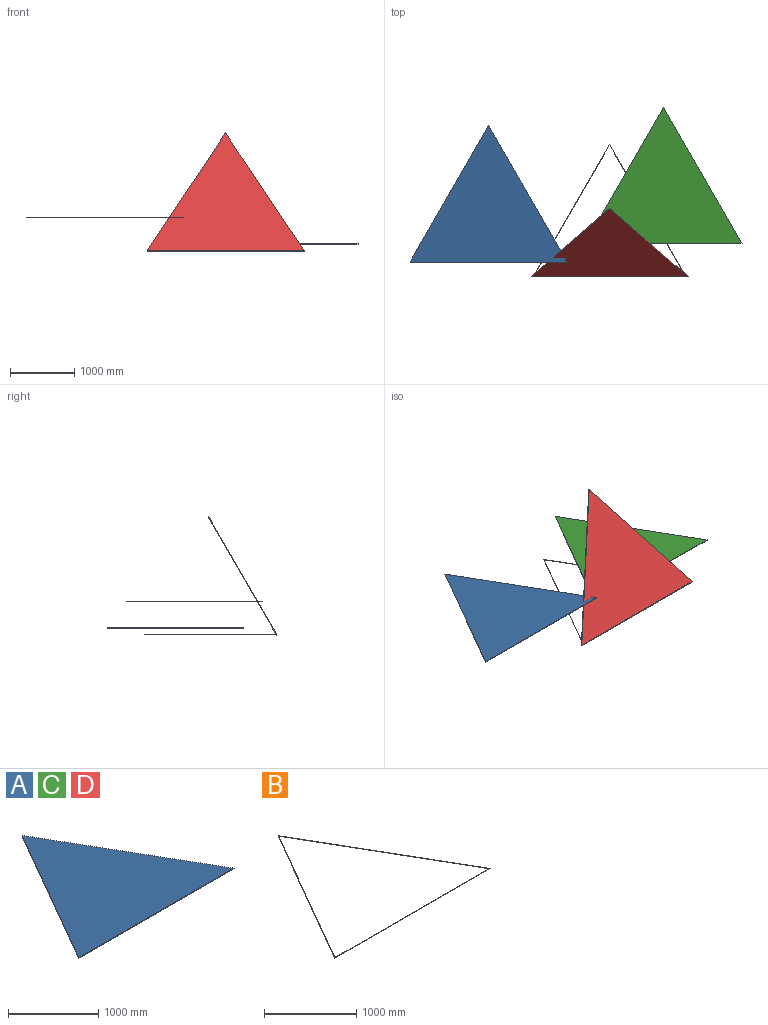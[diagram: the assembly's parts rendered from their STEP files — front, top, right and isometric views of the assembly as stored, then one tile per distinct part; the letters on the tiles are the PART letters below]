
ASSEMBLY  parts=4 mates=1
PART A: 5 faces, bbox 2438.4x2111.7x9.5 mm
  f0: plane 2438.4x9.53mm, normal (0,-1,0), area 23225.8mm2, adj f1,f2,f3,f4
  f1: plane 2111.72x1219.2mm, normal (0.87,0.5,0), area 23225.8mm2, adj f0,f2,f3,f4
  f2: plane 2111.72x1219.2mm, normal (-0.87,0.5,0), area 23225.8mm2, adj f0,f1,f3,f4
  f3: plane 2438.4x2111.72mm, normal (0,0,1), area 2574604.6mm2, adj f0,f1,f2
  f4: plane 2438.4x2111.72mm, normal (0,0,-1), area 2574604.6mm2, adj f0,f1,f2
PART B: 7 faces, bbox 2373.3x2055.4x5.6 mm
  f0: plane 2373.32x5.56mm, normal (0,-0.87,0.5), area 15205.2mm2, adj f1,f2,f4,f5
  f1: plane 2362.2x5.56mm, normal (0,1,0), area 13137.1mm2, adj f0,f3,f4,f6
  f2: plane 2055.36x1186.66mm, normal (-0.75,0.43,0.5), area 15205.2mm2, adj f0,f3,f4,f5
  f3: plane 2045.73x1181.1mm, normal (0.87,-0.5,0), area 13137.1mm2, adj f1,f2,f4,f6
  f4: plane 2373.32x2055.36mm, normal (0,0,-1), area 22807.8mm2, adj f0,f1,f2,f3,f5,f6
  f5: plane 2055.36x1186.66mm, normal (0.75,0.43,0.5), area 15205.2mm2, adj f0,f2,f4,f6
  f6: plane 2045.73x1181.1mm, normal (-0.87,-0.5,0), area 13137.1mm2, adj f1,f3,f4,f5
PART C: same geometry as A
PART D: same geometry as A
PLACE A t=(-2645.18,-529.55,515.03)mm
PLACE B t=(-766.46,-779.3,11.44)mm
PLACE C t=(70.51,-235.25,109.22)mm
PLACE D rot(axis=(1,0,0),60deg) t=(-766.46,-1104.22,610.72)mm
MATE fastened D.f3 <-> B.f0  axis (0,-0.87,0.5) through (-766.46,-1464.42,5.88)mm
